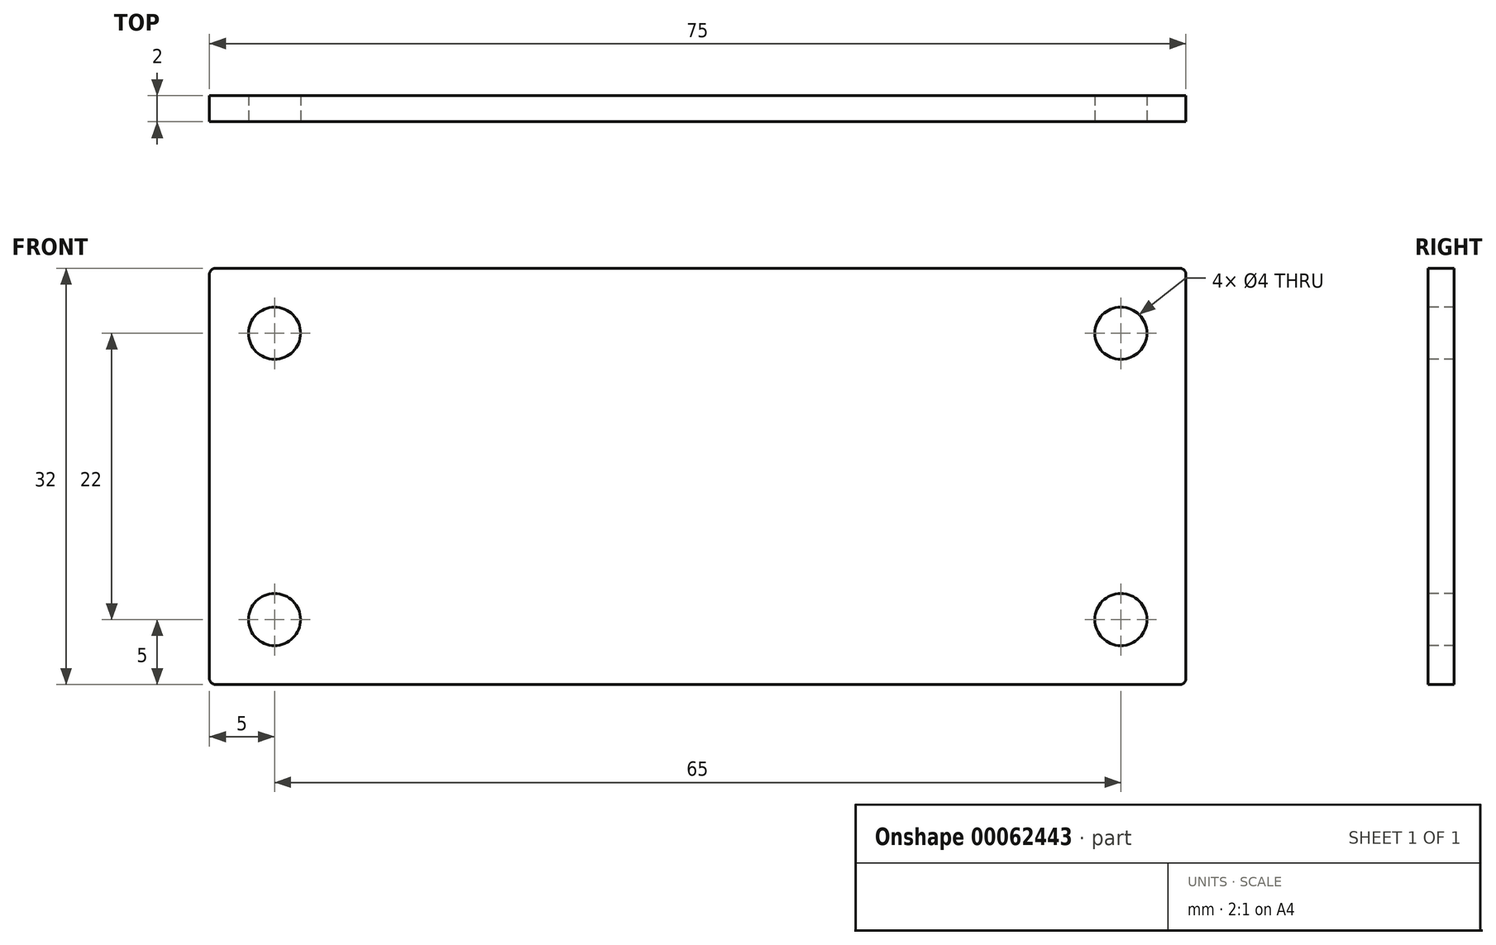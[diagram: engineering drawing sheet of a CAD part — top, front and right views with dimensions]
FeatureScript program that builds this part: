
annotation { "Feature Type Name" : "Feature", "Feature Type Description" : "" }
export const myFeature = defineFeature(function(context is Context, id is Id, definition is map)
    precondition{}
    {
        {
            var Q0;
            Q0=qCreatedBy(makeId("Front.planeOp"),FACE);
            var sketch = newSketch(context, id + "F0", { "sketchPlane" : qUnion([Q0])});
            skLineSegment(sketch, "E0.rect.bottom", {"start": v(37.5, -16) * mm, "end": v(-37.5, -16) * mm});
            skLineSegment(sketch, "E0.rect.top", {"start": v(37.5, 16) * mm, "end": v(-37.5, 16) * mm});
            skLineSegment(sketch, "E0.rect.left", {"start": v(37.5, -16) * mm, "end": v(37.5, 16) * mm});
            skLineSegment(sketch, "E0.rect.right", {"start": v(-37.5, -16) * mm, "end": v(-37.5, 16) * mm});
            skPoint(sketch, "E0.rect.middle", {"position": v(0, 0) * mm});
            skSolve(sketch);
        }
        {
            var Q0;
            Q0=makeQuery(id+"F0.imprint","IMPRINT",FACE,{"disambiguationData":[TD([[makeQuery(id+"F0.imprint","IMPRINT",EDGE,{"derivedFrom":sQuery(id+"F0.wireOp",EDGE,"E0.rect.bottom")}),-1.0]])]});
            extrude(context, id + "F1", {"entities" : qUnion([Q0]), "endBound" : BoundingType.SYMMETRIC, "depth" : 2 * mm});
        }
        {
            var Q0;
            Q0=makeQuery(id+"F1.opExtrude","CAP_FACE",FACE,{"disambiguationData":[OSD([sQuery(id+"F0.wireOp",EDGE,"E0.rect.bottom"),sQuery(id+"F0.wireOp",EDGE,"E0.rect.top"),sQuery(id+"F0.wireOp",EDGE,"E0.rect.left"),sQuery(id+"F0.wireOp",EDGE,"E0.rect.right")])],"isStart":false});
            var sketch = newSketch(context, id + "F2", { "sketchPlane" : qUnion([Q0])});
            skCircle(sketch, "E1", {"center": v(-32.5, 11) * mm, "radius": 2 * mm});
            skCircle(sketch, "E2.MirrorC", {"center": v(-32.5, -11) * mm, "radius": 2 * mm});
            skCircle(sketch, "E3.MirrorC", {"center": v(32.5, -11) * mm, "radius": 2 * mm});
            skCircle(sketch, "E4.MirrorC", {"center": v(32.5, 11) * mm, "radius": 2 * mm});
            skSolve(sketch);
        }
        {
            var Q0;
            Q0 = qSketchRegion(id + "F2", true);
            extrude(context, id + "F3", {"entities" : qUnion([Q0]), "operationType" : NewBodyOperationType.REMOVE, "oppositeDirection" : true, "depth" : 25.4 * mm});
        }
        {
            var Q0;
            Q0=makeQuery(id+"F1.opExtrude","SWEPT_EDGE",EDGE,{"disambiguationData":[OSD([sQuery(id+"F0.wireOp",EDGE,"E0.rect.top"),sQuery(id+"F0.wireOp",EDGE,"E0.rect.left")])]});
            var Q1;
            Q1=makeQuery(id+"F1.opExtrude","SWEPT_EDGE",EDGE,{"disambiguationData":[OSD([sQuery(id+"F0.wireOp",EDGE,"E0.rect.bottom"),sQuery(id+"F0.wireOp",EDGE,"E0.rect.left")])]});
            var Q2;
            Q2=makeQuery(id+"F1.opExtrude","SWEPT_EDGE",EDGE,{"disambiguationData":[OSD([sQuery(id+"F0.wireOp",EDGE,"E0.rect.top"),sQuery(id+"F0.wireOp",EDGE,"E0.rect.right")])]});
            var Q3;
            Q3=makeQuery(id+"F1.opExtrude","SWEPT_EDGE",EDGE,{"disambiguationData":[OSD([sQuery(id+"F0.wireOp",EDGE,"E0.rect.bottom"),sQuery(id+"F0.wireOp",EDGE,"E0.rect.right")])]});
            fillet(context, id + "F4", {"entities" : qUnion([Q0, Q1, Q2, Q3]), "radius" : 0.5 * mm, "tangentPropagation" : true, "allowEdgeOverflow" : false});
        }
    });
